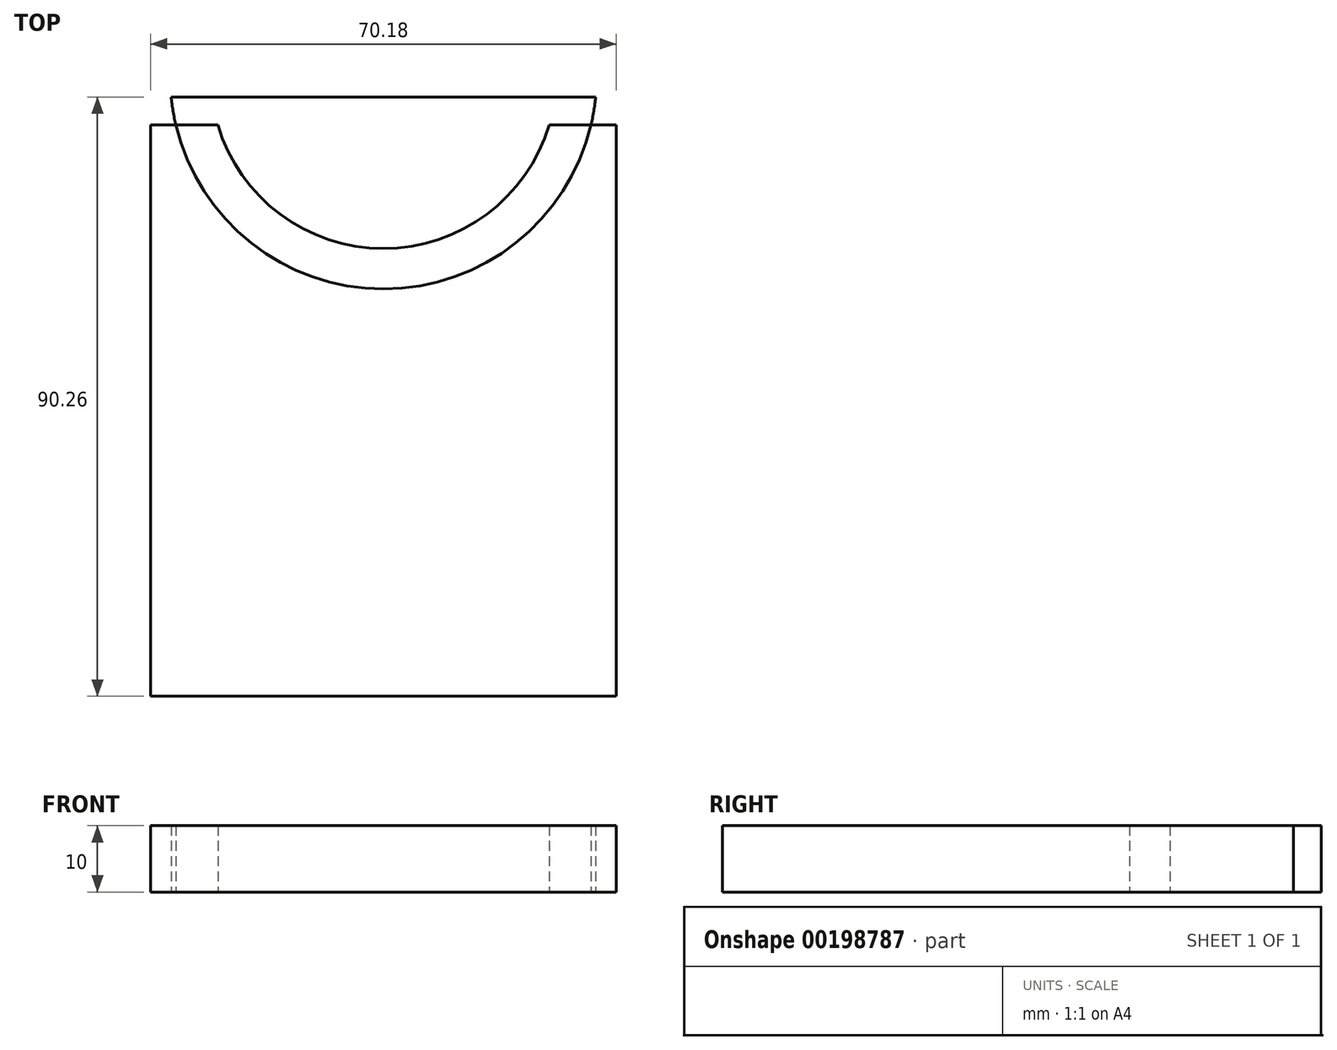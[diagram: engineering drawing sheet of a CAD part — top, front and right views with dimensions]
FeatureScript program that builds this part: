
annotation { "Feature Type Name" : "Feature", "Feature Type Description" : "" }
export const myFeature = defineFeature(function(context is Context, id is Id, definition is map)
    precondition{}
    {
        {
            var Q0;
            Q0=qCreatedBy(makeId("Top.planeOp"),FACE);
            var sketch = newSketch(context, id + "F0", { "sketchPlane" : qUnion([Q0])});
            skLineSegment(sketch, "E0.bottom", {"start": v(-35.1, 46.74) * mm, "end": v(35.1, 46.74) * mm});
            skLineSegment(sketch, "E0.top", {"start": v(-35.1, -46.74) * mm, "end": v(35.1, -46.74) * mm});
            skLineSegment(sketch, "E0.left", {"start": v(-35.1, 46.74) * mm, "end": v(-35.1, -46.74) * mm});
            skLineSegment(sketch, "E0.right", {"start": v(35.1, 46.74) * mm, "end": v(35.1, -46.74) * mm});
            skPoint(sketch, "E0.middle", {"position": v(0, 0) * mm});
            skLineSegment(sketch, "E1.top", {"start": v(-35.1, 39.28) * mm, "end": v(35.1, 39.28) * mm});
            skLineSegment(sketch, "E1.left", {"start": v(-35.1, -46.74) * mm, "end": v(-35.1, 39.28) * mm});
            skLineSegment(sketch, "E1.right", {"start": v(35.1, -46.74) * mm, "end": v(35.1, 39.28) * mm});
            skCircle(sketch, "E2", {"center": v(0, 46.74) * mm, "radius": 32.15 * mm});
            skCircle(sketch, "E3", {"center": v(0, 46.74) * mm, "radius": 26.05 * mm});
            skLineSegment(sketch, "E4.top", {"start": v(-35.1, 43.52) * mm, "end": v(35.1, 43.52) * mm});
            skLineSegment(sketch, "E4.left", {"start": v(-35.1, 39.28) * mm, "end": v(-35.1, 43.52) * mm});
            skLineSegment(sketch, "E4.right", {"start": v(35.1, 39.28) * mm, "end": v(35.1, 43.52) * mm});
            skSolve(sketch);
        }
        {
            var Q0;
            {var subQ0=sQuery(id+"F0.wireOp",EDGE,"E4.top");var subQ1=sQuery(id+"F0.wireOp",EDGE,"E2");var subQ2=makeQuery(id+"F0.imprint","INTERSECT",VERTEX,{"disambiguationData":[OD(0.0)],"derivedFrom":[subQ1,subQ0]});Q0=makeQuery(id+"F0.imprint","IMPRINT",FACE,{"disambiguationData":[TD([[makeQuery(id+"F0.imprint","IMPRINT",EDGE,{"disambiguationData":[TD([[subQ2,-1.0]])],"derivedFrom":subQ1}),1.0]])]});}
            var Q1;
            Q1=makeQuery(id+"F0.imprint","IMPRINT",FACE,{"disambiguationData":[TD([[makeQuery(id+"F0.imprint","IMPRINT",EDGE,{"derivedFrom":sQuery(id+"F0.wireOp",EDGE,"E0.top")}),1.0]])]});
            var Q2;
            {var subQ5=sQuery(id+"F0.wireOp",EDGE,"E4.left");Q2=makeQuery(id+"F0.imprint","IMPRINT",FACE,{"disambiguationData":[TD([[makeQuery(id+"F0.imprint","IMPRINT",EDGE,{"derivedFrom":subQ5}),-1.0]])]});}
            var Q3;
            {var subQ0=sQuery(id+"F0.wireOp",EDGE,"E4.top");var subQ1=sQuery(id+"F0.wireOp",EDGE,"E3");var subQ2=makeQuery(id+"F0.imprint","INTERSECT",VERTEX,{"disambiguationData":[OD(0.0)],"derivedFrom":[subQ1,subQ0]});Q3=makeQuery(id+"F0.imprint","IMPRINT",FACE,{"disambiguationData":[TD([[makeQuery(id+"F0.imprint","IMPRINT",EDGE,{"disambiguationData":[TD([[subQ2,-1.0]])],"derivedFrom":subQ1}),1.0]])]});}
            var Q4;
            {var subQ0=sQuery(id+"F0.wireOp",EDGE,"E1.top");var subQ1=sQuery(id+"F0.wireOp",EDGE,"E2");var subQ2=makeQuery(id+"F0.imprint","INTERSECT",VERTEX,{"disambiguationData":[OD(1.0)],"derivedFrom":[subQ1,subQ0]});Q4=makeQuery(id+"F0.imprint","IMPRINT",FACE,{"disambiguationData":[TD([[makeQuery(id+"F0.imprint","IMPRINT",EDGE,{"disambiguationData":[TD([[subQ2,-1.0]])],"derivedFrom":subQ1}),1.0]])]});}
            var Q5;
            {var subQ5=sQuery(id+"F0.wireOp",EDGE,"E4.right");Q5=makeQuery(id+"F0.imprint","IMPRINT",FACE,{"disambiguationData":[TD([[makeQuery(id+"F0.imprint","IMPRINT",EDGE,{"derivedFrom":subQ5}),1.0]])]});}
            var Q6;
            {var subQ0=sQuery(id+"F0.wireOp",EDGE,"E1.top");var subQ1=sQuery(id+"F0.wireOp",EDGE,"E3");var subQ2=makeQuery(id+"F0.imprint","INTERSECT",VERTEX,{"disambiguationData":[OD(0.0)],"derivedFrom":[subQ1,subQ0]});Q6=makeQuery(id+"F0.imprint","IMPRINT",FACE,{"disambiguationData":[TD([[makeQuery(id+"F0.imprint","IMPRINT",EDGE,{"disambiguationData":[TD([[subQ2,-1.0]])],"derivedFrom":subQ1}),1.0]])]});}
            extrude(context, id + "F1", {"entities" : qUnion([Q0, Q1, Q2, Q3, Q4, Q5, Q6]), "depth" : 10 * mm});
        }
    });
